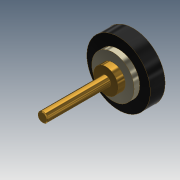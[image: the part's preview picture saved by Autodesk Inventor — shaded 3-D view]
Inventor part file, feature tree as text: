
AUTODESK INVENTOR PART (.ipt)
format: ipt  version: 2017 (Build 210142000, 142)  size: 120,320 bytes
history: native  units: mm
features: other x1, revolve x1, chamfer x1, sketch x1
ambient origin geometry x8: Origin, YZ Plane, XZ Plane, XY Plane, X Axis, Y Axis, Z Axis, Center Point
bodies: Body1 (feature_tree)
feature tree (4):
  other  "Твердое тело1"
  revolve  "Вращение1"
  chamfer  "Фаска1"  Distance=1.4mm
  sketch  "Эскиз1"
